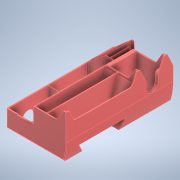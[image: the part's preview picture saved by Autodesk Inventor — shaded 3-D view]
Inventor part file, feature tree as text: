
AUTODESK INVENTOR PART (.ipt)
format: ipt  version: 2021 (Build 250183000, 183)  size: 859,648 bytes
history: native  units: mm
features: projected_geometry x23, extrude x19, sketch x13, fillet x3, plane x2, chamfer x1, other x1
ambient origin geometry x8: Origin, YZ Plane, XZ Plane, XY Plane, X Axis, Y Axis, Z Axis, Center Point
bodies: Solid1 (feature_tree)
feature tree (62):
  extrude  "Extrusion1"  Depth=43.0mm
  plane  "Work Plane1"
  sketch  "Sketch2"  dims[d2=1.0mm d3=1.6mm]
  extrude  "Extrusion2"  Depth=1.6mm
  plane  "Work Plane2"
  extrude  "Extrusion3"  Depth=1.6mm
  extrude  "Extrusion5"  Depth=1.6mm
  sketch  "Sketch4"  dims[d6=1.6mm d7=108.4mm]
  extrude  "Extrusion4"  Depth=31.5mm
  extrude  "Extrusion6"  Depth=63.0mm
  extrude  "Extrusion7"  Depth=0.5mm
  extrude  "Extrusion8"  Depth=13.0mm
  extrude  "Extrusion12"  TaperAngle=0.0deg  [1 undecoded]
  extrude  "Extrusion10"  Depth=0.25mm
  extrude  "Extrusion11"  Depth=0.25mm
  extrude  "Extrusion13"  Depth=61.0mm
  extrude  "Extrusion14"  Depth=1.0mm
  extrude  "Extrusion15"  Depth=1.0mm
  chamfer  "Chamfer1"  Distance=1.0mm
  fillet  "Fillet1"  [1 undecoded]
  fillet  "Fillet2"  Radius=10.0mm
  extrude  "Extrusion16"  Depth=1.0mm
  extrude  "Extrusion17"  Depth=0.5mm TaperAngle=0.0deg
  sketch  "Sketch14"  dims[d24=0.25mm d25=61.0mm]
  extrude  "Extrusion18"  Depth=0.5mm
  extrude  "Extrusion19"  Depth=0.5mm
  fillet  "Fillet3"  Radius=1.0mm
  sketch  "Sketch1"  dims[d0=30.0mm d1=43.0mm]
  projected_geometry  "Projected Loop1"
  projected_geometry  "Projected Loop2"
  sketch  "Sketch3"  dims[d4=1.6mm d5=1.6mm]
  projected_geometry  "Projected Loop3"
  projected_geometry  "Projected Loop4"
  sketch  "Sketch7"  dims[d8=51.0mm d9=31.5mm]
  sketch  "Sketch8"  dims[d10=18.2mm d11=63.0mm]
  projected_geometry  "Projected Loop13"
  projected_geometry  "Projected Loop14"
  projected_geometry  "Projected Loop15"
  sketch  "Sketch9"  dims[d14=0.5mm d15=86.937881mm]
  projected_geometry  "Projected Loop16"
  sketch  "Sketch10"  dims[d16=86.937881mm d17=13.0mm]
  projected_geometry  "Projected Loop17"
  projected_geometry  "Projected Loop18"
  sketch  "Sketch11"  dims[d18=177.75mm d19=0.0mm]
  projected_geometry  "Projected Loop19"
  sketch  "Sketch12"  dims[d20=-1.6mm d21=0.25mm]
  projected_geometry  "Projected Loop20"
  projected_geometry  "Projected Loop21"
  sketch  "Sketch13"  dims[d22=101.0mm d23=0.25mm]
  projected_geometry  "Projected Loop22"
  projected_geometry  "Projected Loop23"
  projected_geometry  "Projected Loop24"
  projected_geometry  "Projected Loop25"
  projected_geometry  "Projected Loop26"
  projected_geometry  "Projected Loop27"
  projected_geometry  "Projected Loop28"
  projected_geometry  "Projected Loop29"
  sketch  "Sketch15"  dims[d26=2.398948mm d27=1.0mm d28=1.0mm d29=1.0mm d30=0.0mm d31=10.0mm d32=0.0mm d36=1.0mm d38=54.2mm d39=0.0mm d40=55.2mm d44=0.8mm d45=1.0mm d47=224.0mm d49=0.25mm d50=42.0mm d51=0.0mm d52=43.0mm d53=65.0mm d54=0.8mm d55=43.0mm d56=1.398948mm d57=43.0mm d58=0.8mm d60=8.0mm d61=40.0mm d63=9.2mm d64=10.0mm d66=10.0mm d68=46.2mm d69=0.0mm d70=38.2mm d71=0.0mm d72=30.2mm d73=0.0mm d74=1.95mm d75=1.6mm d79=25.2mm d80=30.2mm d81=0.0mm d82=26.2mm d83=0.0mm d84=6.0mm d85=1.2mm d86=30.2mm d87=0.0mm d88=20.0mm d89=15.0mm d90=0.0mm d91=0.0mm d92=20.0mm d93=22.2mm d94=0.0mm d95=22.2mm d96=0.0mm d97=3.0mm d98=2.0mm d99=45.0deg d100=1.2mm d101=0.25mm d102=0.5mm d103=5.0mm d104=1.0mm d105=0.25mm d106=22.2mm d107=0.0mm d108=26.75mm d109=22.2mm d110=0.0mm d111=18.0mm d112=5.0mm d113=20.038534mm d115=20.038534mm d116=22.2mm d117=0.0mm d118=5.0mm d119=120.0deg d120=0.0mm d121=0.0mm d122=22.2mm d123=0.0mm d124=1.0mm d125=5.0mm d126=0.5mm d127=1.6mm d76=0.5mm d77=0.872665mm d78=0.5mm]
  projected_geometry  "Projected Loop30"
  other  "Srf1"
  projected_geometry  "Projected Loop31"
  extrude  "ExtrusionSrf1"  Depth=0.5mm
note: 2 required parameter values undecoded (feature->parameter linkage not recoverable at this tier; creation-order binding heuristic only, values carry confidence <= 0.55)
